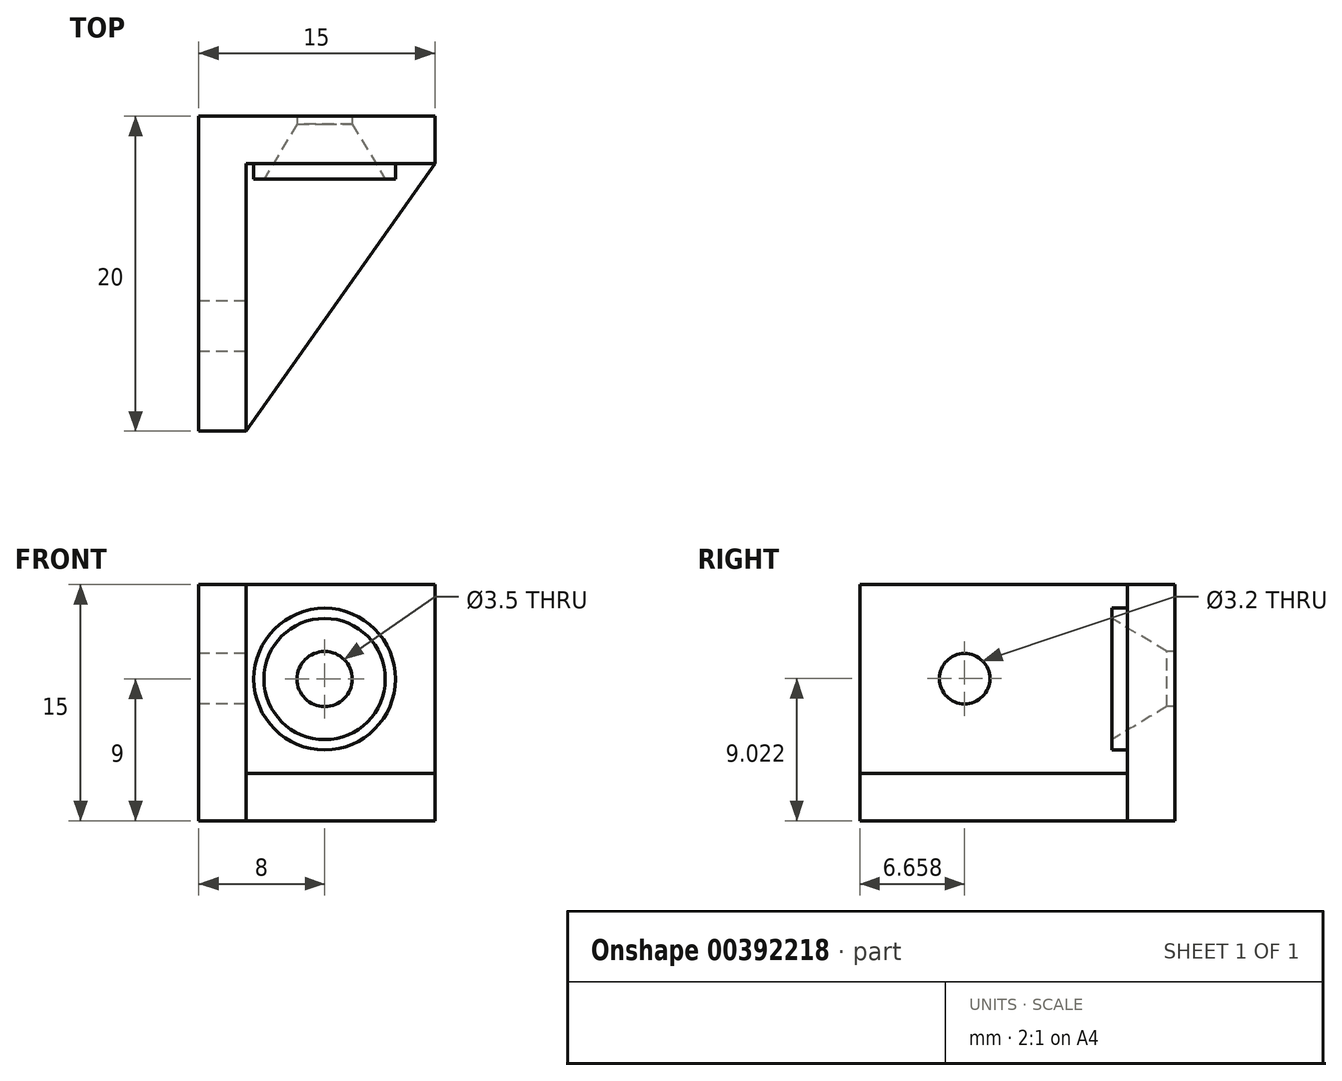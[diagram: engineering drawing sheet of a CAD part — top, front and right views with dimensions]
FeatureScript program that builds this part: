
annotation { "Feature Type Name" : "Feature", "Feature Type Description" : "" }
export const myFeature = defineFeature(function(context is Context, id is Id, definition is map)
    precondition{}
    {
        {
            var Q0;
            Q0=qCreatedBy(makeId("Top.planeOp"),FACE);
            var sketch = newSketch(context, id + "F0", { "sketchPlane" : qUnion([Q0])});
            skPoint(sketch, "E0.middle", {"position": v(0, 0) * mm});
            skLineSegment(sketch, "E1.top", {"start": v(7.5, 10) * mm, "end": v(-7.5, 10) * mm});
            skLineSegment(sketch, "E1.right", {"start": v(-7.5, -10) * mm, "end": v(-7.5, 10) * mm});
            skLineSegment(sketch, "E2.0", {"start": v(7.5, 7) * mm, "end": v(-7.5, 7) * mm});
            skLineSegment(sketch, "E3.0", {"start": v(-4.5, -10) * mm, "end": v(-4.5, 10) * mm});
            skLineSegment(sketch, "E4", {"start": v(-4.5, -10) * mm, "end": v(7.5, 7) * mm});
            skLineSegment(sketch, "E5", {"start": v(7.5, 10) * mm, "end": v(7.5, 7) * mm});
            skLineSegment(sketch, "E6", {"start": v(-4.5, -10) * mm, "end": v(-7.5, -10) * mm});
            skSolve(sketch);
        }
        {
            var Q0;
            {var subQ0=sQuery(id+"F0.wireOp",EDGE,"E4");Q0=makeQuery(id+"F0.imprint","IMPRINT",FACE,{"disambiguationData":[TD([[makeQuery(id+"F0.imprint","IMPRINT",EDGE,{"derivedFrom":subQ0}),1.0]])]});}
            extrude(context, id + "F1", {"entities" : qUnion([Q0]), "depth" : 3 * mm});
        }
        {
            var Q0;
            {var subQ0=sQuery(id+"F0.wireOp",EDGE,"E5");Q0=makeQuery(id+"F0.imprint","IMPRINT",FACE,{"disambiguationData":[TD([[makeQuery(id+"F0.imprint","IMPRINT",EDGE,{"derivedFrom":subQ0}),-1.0]])]});}
            var Q1;
            {var subQ0=sQuery(id+"F0.wireOp",EDGE,"E1.right");var subQ1=sQuery(id+"F0.wireOp",EDGE,"E1.top");var subQ2=makeQuery(id+"F0.imprint","INTERSECT",VERTEX,{"derivedFrom":[subQ1,subQ0]});Q1=makeQuery(id+"F0.imprint","IMPRINT",FACE,{"disambiguationData":[TD([[makeQuery(id+"F0.imprint","IMPRINT",EDGE,{"disambiguationData":[TD([[subQ2,1.0]])],"derivedFrom":subQ1}),1.0]])]});}
            var Q2;
            {var subQ0=sQuery(id+"F0.wireOp",EDGE,"E6");Q2=makeQuery(id+"F0.imprint","IMPRINT",FACE,{"disambiguationData":[TD([[makeQuery(id+"F0.imprint","IMPRINT",EDGE,{"derivedFrom":subQ0}),-1.0]])]});}
            extrude(context, id + "F2", {"entities" : qUnion([Q0, Q1, Q2]), "operationType" : NewBodyOperationType.ADD, "depth" : 15 * mm});
        }
        {
            var Q0;
            Q0=makeQuery(id+"F2.opExtrude","SWEPT_FACE",FACE,{"disambiguationData":[OSD([sQuery(id+"F0.wireOp",EDGE,"E2.0")])]});
            var sketch = newSketch(context, id + "F3", { "sketchPlane" : qUnion([Q0])});
            skCircle(sketch, "E7", {"center": v(0.5, 9) * mm, "radius": 4.5 * mm});
            skLineSegment(sketch, "E8", {"start": v(0.5, 3) * mm, "end": v(0.5, 15) * mm, "construction": true});
            skCircle(sketch, "E9", {"center": v(0.5, 9) * mm, "radius": 1.75 * mm});
            skCircle(sketch, "E10", {"center": v(0.5, 9) * mm, "radius": 3.5 * mm});
            skLineSegment(sketch, "E11", {"start": v(0.5, 9) * mm, "end": v(-7.5, 9) * mm, "construction": true});
            skPoint(sketch, "E11.endSnap0", {"position": v(-4.5, 9) * mm});
            skSolve(sketch);
        }
        {
            var Q0;
            Q0=makeQuery(id+"F3.imprint","IMPRINT",FACE,{"disambiguationData":[TD([[makeQuery(id+"F3.imprint","IMPRINT",EDGE,{"derivedFrom":sQuery(id+"F3.wireOp",EDGE,"E9")}),1.0]])]});
            extrude(context, id + "F4", {"entities" : qUnion([Q0]), "operationType" : NewBodyOperationType.REMOVE, "oppositeDirection" : true, "depth" : 25 * mm});
        }
        {
            var Q0;
            Q0=makeQuery(id+"F3.imprint","IMPRINT",FACE,{"disambiguationData":[TD([[makeQuery(id+"F3.imprint","IMPRINT",EDGE,{"derivedFrom":sQuery(id+"F3.wireOp",EDGE,"E7")}),1.0]])]});
            extrude(context, id + "F5", {"entities" : qUnion([Q0]), "operationType" : NewBodyOperationType.ADD, "depth" : 1 * mm});
        }
        {
            var Q0;
            Q0=makeQuery(id+"F3.imprint","IMPRINT",FACE,{"disambiguationData":[TD([[makeQuery(id+"F3.imprint","IMPRINT",EDGE,{"derivedFrom":sQuery(id+"F3.wireOp",EDGE,"E9")}),-1.0]])]});
            extrude(context, id + "F6", {"entities" : qUnion([Q0]), "operationType" : NewBodyOperationType.ADD, "depth" : 1 * mm});
        }
        {
            var Q0;
            Q0=makeQuery(id+"F6.opExtrude","CAP_EDGE",EDGE,{"disambiguationData":[OSD([sQuery(id+"F3.wireOp",EDGE,"E9")])],"isStart":false});
            chamfer(context, id + "F7", {"entities" : qUnion([Q0]), "chamferType" : ChamferType.TWO_OFFSETS, "width1" : 3.5 * mm, "oppositeDirection" : false, "width2" : 2.1 * mm, "tangentPropagation" : true});
        }
        {
            var Q0;
            Q0=makeQuery(id+"F2.opExtrude","SWEPT_FACE",FACE,{"disambiguationData":[OSD([sQuery(id+"F0.wireOp",EDGE,"E1.right")])]});
            var sketch = newSketch(context, id + "F8", { "sketchPlane" : qUnion([Q0])});
            skLineSegment(sketch, "E12", {"start": v(-6.97, 9.02) * mm, "end": v(10, 9.02) * mm, "construction": true});
            skCircle(sketch, "E13", {"center": v(3.34, 9.02) * mm, "radius": 1.6 * mm});
            skSolve(sketch);
        }
        {
            var Q0;
            Q0=qSketchRegion(id+"F8",true);
            extrude(context, id + "F9", {"entities" : qUnion([Q0]), "operationType" : NewBodyOperationType.REMOVE, "oppositeDirection" : true, "depth" : 25 * mm});
        }
    });
